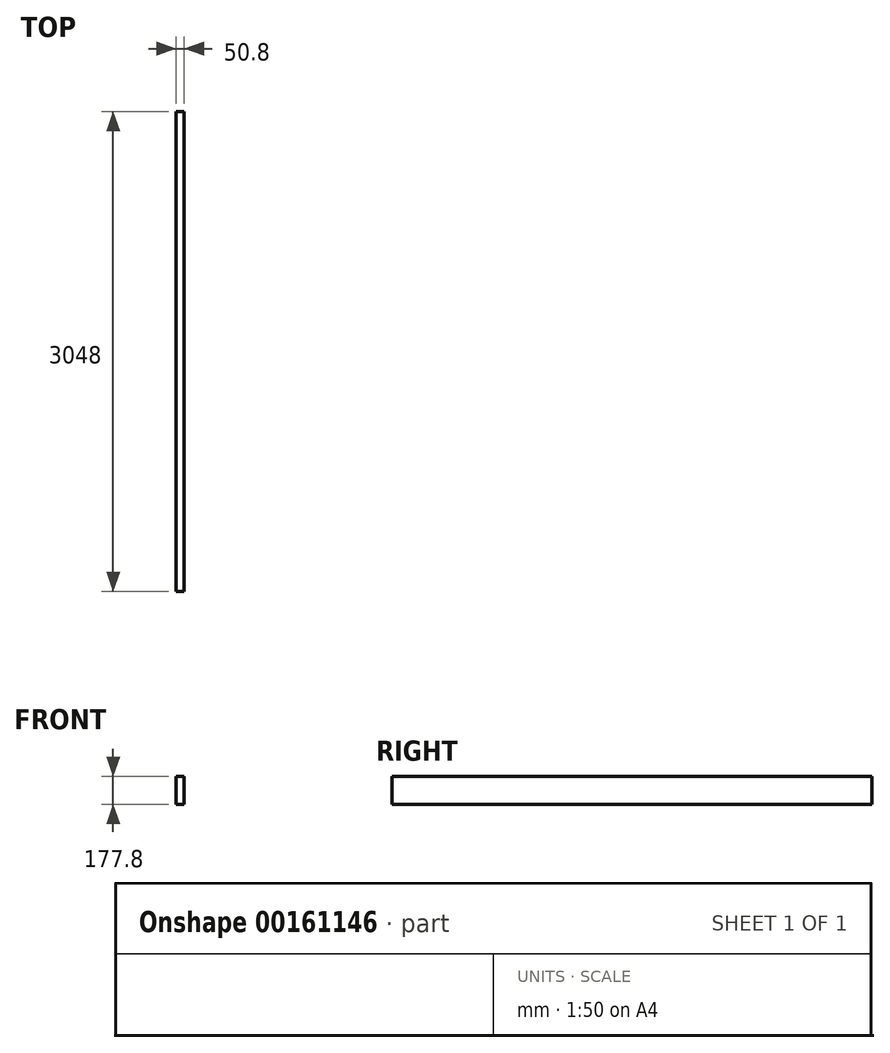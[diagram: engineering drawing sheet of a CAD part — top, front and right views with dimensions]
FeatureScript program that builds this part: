
annotation { "Feature Type Name" : "Feature", "Feature Type Description" : "" }
export const myFeature = defineFeature(function(context is Context, id is Id, definition is map)
    precondition{}
    {
        {
            var Q0;
            Q0=qCreatedBy(makeId("Front.planeOp"),FACE);
            var sketch = newSketch(context, id + "F0", { "sketchPlane" : qUnion([Q0])});
            skLineSegment(sketch, "E0.bottom", {"start": v(0, 0) * mm, "end": v(50.8, 0) * mm});
            skLineSegment(sketch, "E0.top", {"start": v(0, 177.8) * mm, "end": v(50.8, 177.8) * mm});
            skLineSegment(sketch, "E0.left", {"start": v(0, 0) * mm, "end": v(0, 177.8) * mm});
            skLineSegment(sketch, "E0.right", {"start": v(50.8, 0) * mm, "end": v(50.8, 177.8) * mm});
            skSolve(sketch);
        }
        {
            var Q0;
            Q0=qSketchRegion(id+"F0",true);
            extrude(context, id + "F1", {"entities" : qUnion([Q0]), "depth" : 3048 * mm});
        }
    });
